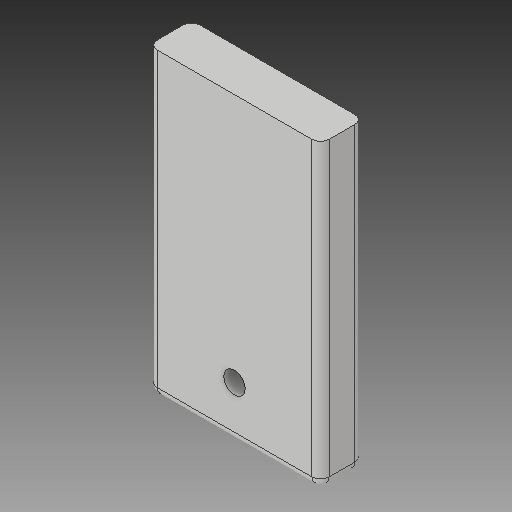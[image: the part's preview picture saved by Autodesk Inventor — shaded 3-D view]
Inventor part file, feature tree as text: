
AUTODESK INVENTOR PART (.ipt)
format: ipt  version: 2018 (Build 220112000, 112)  size: 110,592 bytes
history: native  units: mm
features: other x3, fillet x2, sketch x1, plane x1, extrude x1, reference x1
ambient origin geometry x8: Origin, YZ Plane, XZ Plane, XY Plane, X Axis, Y Axis, Z Axis, Center Point
bodies: Solid1 (feature_tree)
feature tree (9):
  sketch  "Sketch1"  dims[d0=10.0mm d1=0.0mm d2=1.0mm d3=1.0mm]
  plane  "Work Plane1"
  extrude  "Extrusion1"  Depth=1.0mm
  fillet  "Fillet1"  Radius=1.0mm
  fillet  "Fillet2"  [1 undecoded]
  reference  "Reference1"
  other  "<userpath>\OneDrive\Documents\Inventor\TSA\2018\Animatronics\Tortoise\Turtle3.iam"
  other  "Turtle3.iam"
  other  "HeadBottom:1"
note: 1 required parameter value undecoded (feature->parameter linkage not recoverable at this tier; creation-order binding heuristic only, values carry confidence <= 0.55)
